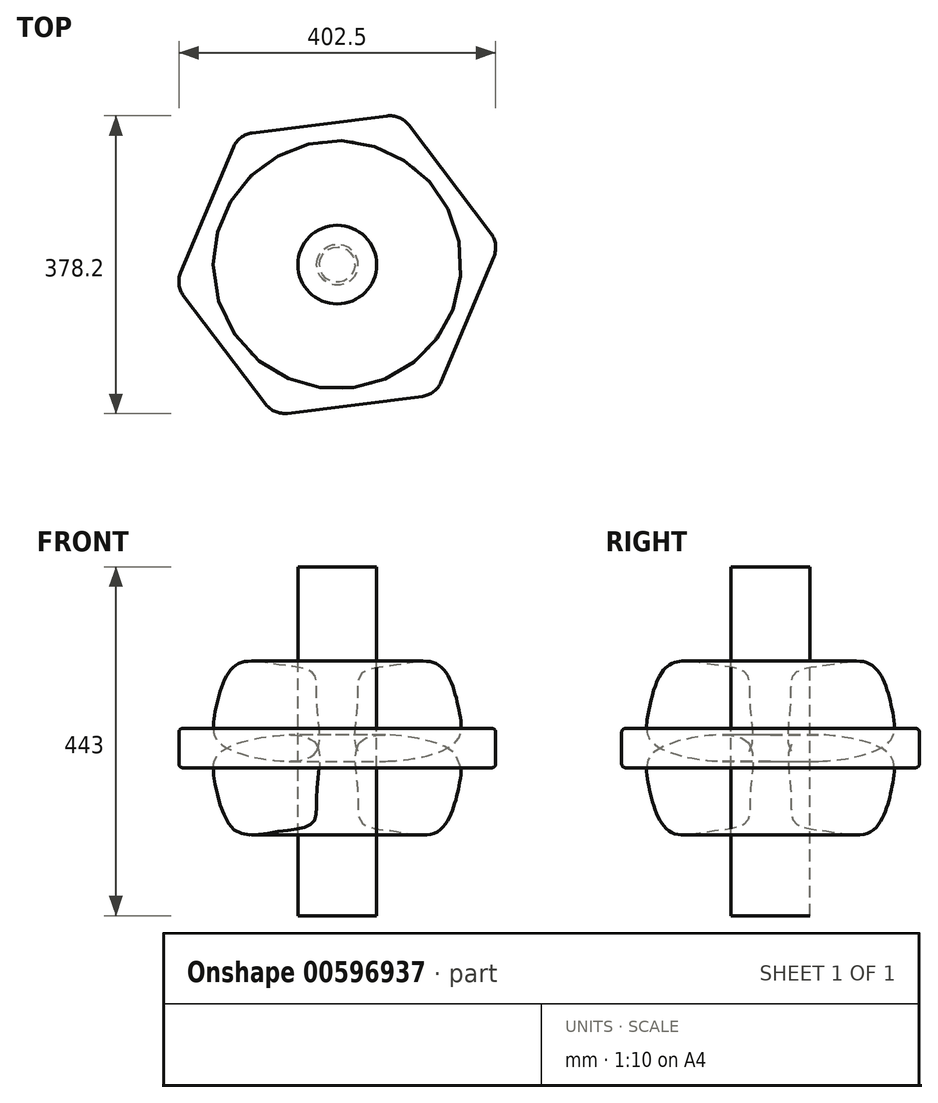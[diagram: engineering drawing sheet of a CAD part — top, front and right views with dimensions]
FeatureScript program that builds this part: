
annotation { "Feature Type Name" : "Feature", "Feature Type Description" : "" }
export const myFeature = defineFeature(function(context is Context, id is Id, definition is map)
    precondition{}
    {
        {
            var Q0;
            Q0=qCreatedBy(makeId("Front.planeOp"),FACE);
            var sketch = newSketch(context, id + "F0", { "sketchPlane" : qUnion([Q0])});
            skFitSpline(sketch, "E0", {"points": [v(25.96, -75.65) * mm, v(82.07, -74.33) * mm, v(87.27, -8.3) * mm, v(81.7, 28.5) * mm, v(103.98, 52.84) * mm, v(77.06, 67.56) * mm, v(30.75, 57.75) * mm, v(17.25, 41.47) * mm, v(19.72, 11.25) * mm, v(25.72, -38.3) * mm, v(12.8, -54.55) * mm, v(25.96, -75.65) * mm]});
            skSolve(sketch);
        }
        {
            var Q0;
            Q0=qCreatedBy(makeId("Front.planeOp"),FACE);
            var sketch = newSketch(context, id + "F1", { "sketchPlane" : qUnion([Q0])});
            skLineSegment(sketch, "E1", {"start": v(0, 0) * mm, "end": v(0, -103.86) * mm});
            skSolve(sketch);
        }
        {
            var Q0;
            Q0=sQuery(id+"F0.wireOp",EDGE,"E0");
            var Q1;
            Q1=sQuery(id+"F1.wireOp",EDGE,"E1");
            revolve(context, id + "F2", {"bodyType" : ToolBodyType.SURFACE, "surfaceEntities" : qUnion([Q0]), "axis" : qUnion([Q1]), "revolveType" : RevolveType.FULL});
        }
        {
            var Q0;
            Q0=qCreatedBy(makeId("Front.planeOp"),FACE);
            var sketch = newSketch(context, id + "F3", { "sketchPlane" : qUnion([Q0])});
            skFitSpline(sketch, "E2", {"points": [v(-26.6, -134.35) * mm, v(-25.95, -72.85) * mm, v(-30.9, -35.1) * mm, v(-73.18, -24.31) * mm, v(-128.65, -24.5) * mm, v(-155.06, -84.15) * mm, v(-150.94, -121.96) * mm, v(-78.29, -145.77) * mm, v(-26.6, -134.35) * mm]});
            skSolve(sketch);
        }
        {
            var Q0;
            Q0=makeQuery(id+"F3.imprint","IMPRINT",FACE,{"disambiguationData":[TD([[makeQuery(id+"F3.imprint","IMPRINT",EDGE,{"derivedFrom":sQuery(id+"F3.wireOp",EDGE,"E2")}),1.0]])]});
            var Q1;
            Q1=sQuery(id+"F1.wireOp",EDGE,"E1");
            revolve(context, id + "F4", {"entities" : qUnion([Q0]), "axis" : qUnion([Q1]), "revolveType" : RevolveType.FULL, "oppositeDirection" : true});
        }
        {
            var Q0;
            Q0=qCreatedBy(makeId("Top.planeOp"),FACE);
            cPlane(context, id + "F5", {"entities" : qUnion([Q0]), "cplaneType" : CPlaneType.OFFSET, "offset" : 130 * mm, "oppositeDirection" : true, "width" : 150 * mm, "height" : 150 * mm});
        }
        {
            var Q0;
            Q0=makeQuery(id+"F4.opRevolve","SWEPT_BODY",BODY,{"disambiguationData":[OSD([sQuery(id+"F3.wireOp",EDGE,"E2")])]});
            var Q1;
            Q1=makeQuery(id+"F2.opRevolve","SWEPT_BODY",BODY,{"disambiguationData":[OSD([sQuery(id+"F0.wireOp",EDGE,"E0")])]});
            var Q2;
            Q2=qCreatedBy(id+"F5.planeOp",FACE);
            mirror(context, id + "F6", {"entities" : qUnion([Q0, Q1]), "mirrorPlane" : qUnion([Q2])});
        }
        {
            var Q0;
            Q0=qCreatedBy(id+"F5.planeOp",FACE);
            var sketch = newSketch(context, id + "F7", { "sketchPlane" : qUnion([Q0])});
            skCircle(sketch, "E3.cCircle", {"center": v(0, 0) * mm, "radius": 207.25 * mm, "construction": true});
            skLineSegment(sketch, "E3.0", {"start": v(205.62, 25.92) * mm, "end": v(125.26, -165.11) * mm});
            skLineSegment(sketch, "E3.1", {"start": v(125.26, -165.11) * mm, "end": v(-80.36, -191.03) * mm});
            skLineSegment(sketch, "E3.2", {"start": v(-80.36, -191.03) * mm, "end": v(-205.62, -25.92) * mm});
            skLineSegment(sketch, "E3.3", {"start": v(-205.62, -25.92) * mm, "end": v(-125.26, 165.11) * mm});
            skLineSegment(sketch, "E3.4", {"start": v(-125.26, 165.11) * mm, "end": v(80.36, 191.03) * mm});
            skLineSegment(sketch, "E3.5", {"start": v(80.36, 191.03) * mm, "end": v(205.62, 25.92) * mm});
            skSolve(sketch);
        }
        {
            var Q0;
            Q0=makeQuery(id+"F7.imprint","IMPRINT",FACE,{"disambiguationData":[TD([[makeQuery(id+"F7.imprint","IMPRINT",EDGE,{"derivedFrom":sQuery(id+"F7.wireOp",EDGE,"E3.0")}),-1.0]])]});
            extrude(context, id + "F8", {"entities" : qUnion([Q0]), "endBound" : BoundingType.SYMMETRIC, "depth" : 50 * mm, "offsetDistance" : 25 * mm});
        }
        {
            var Q0;
            Q0=makeQuery(id+"F8.opExtrude","SWEPT_EDGE",EDGE,{"disambiguationData":[OSD([sQuery(id+"F7.wireOp",EDGE,"E3.0"),sQuery(id+"F7.wireOp",EDGE,"E3.1")])]});
            var Q1;
            Q1=makeQuery(id+"F8.opExtrude","SWEPT_EDGE",EDGE,{"disambiguationData":[OSD([sQuery(id+"F7.wireOp",EDGE,"E3.1"),sQuery(id+"F7.wireOp",EDGE,"E3.2")])]});
            var Q2;
            Q2=makeQuery(id+"F8.opExtrude","SWEPT_EDGE",EDGE,{"disambiguationData":[OSD([sQuery(id+"F7.wireOp",EDGE,"E3.2"),sQuery(id+"F7.wireOp",EDGE,"E3.3")])]});
            var Q3;
            Q3=makeQuery(id+"F8.opExtrude","SWEPT_EDGE",EDGE,{"disambiguationData":[OSD([sQuery(id+"F7.wireOp",EDGE,"E3.3"),sQuery(id+"F7.wireOp",EDGE,"E3.4")])]});
            var Q4;
            Q4=makeQuery(id+"F8.opExtrude","SWEPT_EDGE",EDGE,{"disambiguationData":[OSD([sQuery(id+"F7.wireOp",EDGE,"E3.4"),sQuery(id+"F7.wireOp",EDGE,"E3.5")])]});
            var Q5;
            Q5=makeQuery(id+"F8.opExtrude","SWEPT_EDGE",EDGE,{"disambiguationData":[OSD([sQuery(id+"F7.wireOp",EDGE,"E3.0"),sQuery(id+"F7.wireOp",EDGE,"E3.5")])]});
            fillet(context, id + "F9", {"entities" : qUnion([Q0, Q1, Q2, Q3, Q4, Q5]), "radius" : 30 * mm, "tangentPropagation" : true, "allowEdgeOverflow" : false});
        }
        {
            var Q0;
            Q0=makeQuery(id+"F8.opExtrude","CAP_EDGE",EDGE,{"disambiguationData":[OSD([sQuery(id+"F7.wireOp",EDGE,"E3.1")])],"isStart":true});
            var Q1;
            {var subQ0=sQuery(id+"F7.wireOp",EDGE,"E3.2");var subQ1=sQuery(id+"F7.wireOp",EDGE,"E3.1");Q1=makeQuery(id+"F9.opFillet","BLEND_EDGE",EDGE,{"blendedFrom":[makeQuery(id+"F8.opExtrude","SWEPT_EDGE",EDGE,{"disambiguationData":[OSD([subQ1,subQ0])]}),makeQuery(id+"F8.opExtrude","CAP_FACE",FACE,{"disambiguationData":[OSD([sQuery(id+"F7.wireOp",EDGE,"E3.0"),subQ1,subQ0,sQuery(id+"F7.wireOp",EDGE,"E3.3"),sQuery(id+"F7.wireOp",EDGE,"E3.4"),sQuery(id+"F7.wireOp",EDGE,"E3.5")])],"isStart":true})],"blendedInto":[makeQuery(id+"F8.opExtrude","CAP_FACE",FACE,{"disambiguationData":[OSD([sQuery(id+"F7.wireOp",EDGE,"E3.0"),subQ1,subQ0,sQuery(id+"F7.wireOp",EDGE,"E3.3"),sQuery(id+"F7.wireOp",EDGE,"E3.4"),sQuery(id+"F7.wireOp",EDGE,"E3.5")])],"isStart":true})]});}
            var Q2;
            Q2=makeQuery(id+"F8.opExtrude","CAP_FACE",FACE,{"disambiguationData":[OSD([sQuery(id+"F7.wireOp",EDGE,"E3.0"),sQuery(id+"F7.wireOp",EDGE,"E3.1"),sQuery(id+"F7.wireOp",EDGE,"E3.2"),sQuery(id+"F7.wireOp",EDGE,"E3.3"),sQuery(id+"F7.wireOp",EDGE,"E3.4"),sQuery(id+"F7.wireOp",EDGE,"E3.5")])],"isStart":true});
            var Q3;
            Q3=makeQuery(id+"F8.opExtrude","CAP_FACE",FACE,{"disambiguationData":[OSD([sQuery(id+"F7.wireOp",EDGE,"E3.0"),sQuery(id+"F7.wireOp",EDGE,"E3.1"),sQuery(id+"F7.wireOp",EDGE,"E3.2"),sQuery(id+"F7.wireOp",EDGE,"E3.3"),sQuery(id+"F7.wireOp",EDGE,"E3.4"),sQuery(id+"F7.wireOp",EDGE,"E3.5")])],"isStart":false});
            fillet(context, id + "F10", {"entities" : qUnion([Q0, Q1, Q2, Q3]), "radius" : 5 * mm, "tangentPropagation" : true, "allowEdgeOverflow" : false});
        }
        {
            var Q0;
            Q0=qCreatedBy(makeId("Top.planeOp"),FACE);
            cPlane(context, id + "F11", {"entities" : qUnion([Q0]), "cplaneType" : CPlaneType.OFFSET, "offset" : 100 * mm, "width" : 150 * mm, "height" : 150 * mm});
        }
        {
            var Q0;
            Q0=qCreatedBy(id+"F11.planeOp",FACE);
            var sketch = newSketch(context, id + "F12", { "sketchPlane" : qUnion([Q0])});
            skCircle(sketch, "E4", {"center": v(0, 0) * mm, "radius": 50 * mm});
            skSolve(sketch);
        }
        {
            var Q0;
            Q0=makeQuery(id+"F12.imprint","IMPRINT",FACE,{"disambiguationData":[TD([[makeQuery(id+"F12.imprint","IMPRINT",EDGE,{"derivedFrom":sQuery(id+"F12.wireOp",EDGE,"E4")}),1.0]])]});
            var Q1;
            Q1=sQuery(id+"F12.wireOp",EDGE,"E4");
            extrude(context, id + "F13", {"entities" : qUnion([Q0]), "surfaceEntities" : qUnion([Q1]), "oppositeDirection" : true, "depth" : 443 * mm, "offsetDistance" : 25 * mm});
        }
    });
